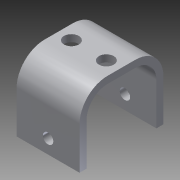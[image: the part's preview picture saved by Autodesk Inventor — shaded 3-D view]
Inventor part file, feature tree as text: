
AUTODESK INVENTOR PART (.ipt)
format: ipt  version: 2013 (Build 170138000, 138)  size: 164,864 bytes
history: native  units: in
note: dims shown in document units (in); Inventor stores cm internally (conversion verified against a paired STEP export)
features: sheet_metal_op x7, sketch x6, other x5, projected_geometry x1
ambient origin geometry x8: Origin, YZ Plane, XZ Plane, XY Plane, X Axis, Y Axis, Z Axis, Center Point
bodies: Solid1 (feature_tree)
feature tree (19):
  sheet_metal_op  "Face1"
  sheet_metal_op  "Flange3"
  sheet_metal_op  "Flange4"
  sketch  "Sketch9"  dims[d29=0.125in d30=0.0625in d31=0.25in d32=0.125in d33=1.0in d34=90.0deg d35=0.375in d36=0.5in d37=0.125in d38=0.125in d39=0.125in d40=0.0625in d41=0.25in d42=0.125in d43=1.25in d44=90.0deg d45=0.375in d46=0.5in d47=0.125in d48=0.125in d49=0.125in d50=0.0in d51=0.25in d52=0.266in d53=0.25in d54=0.266in d55=0.125in d56=0.0in]
  sketch  "Sketch1"  dims[d0=1.125in]
  other  "Plate1"
  sketch  "Sketch5"  dims[d1=0.75in]
  other  "Plate4"
  sheet_metal_op  "Bend3"
  sheet_metal_op  "Corner3"
  sketch  "Sketch6"  dims[d2=0.25in]
  other  "Plate5"
  sheet_metal_op  "Bend4"
  sheet_metal_op  "Corner4"
  sketch  "Sketch7"  dims[d3=0.1875in]
  projected_geometry  "Projected Loop1"
  sketch  "Sketch8"  dims[d4=0.125in]
  other  "Cut2"
  other  "Cut3"
